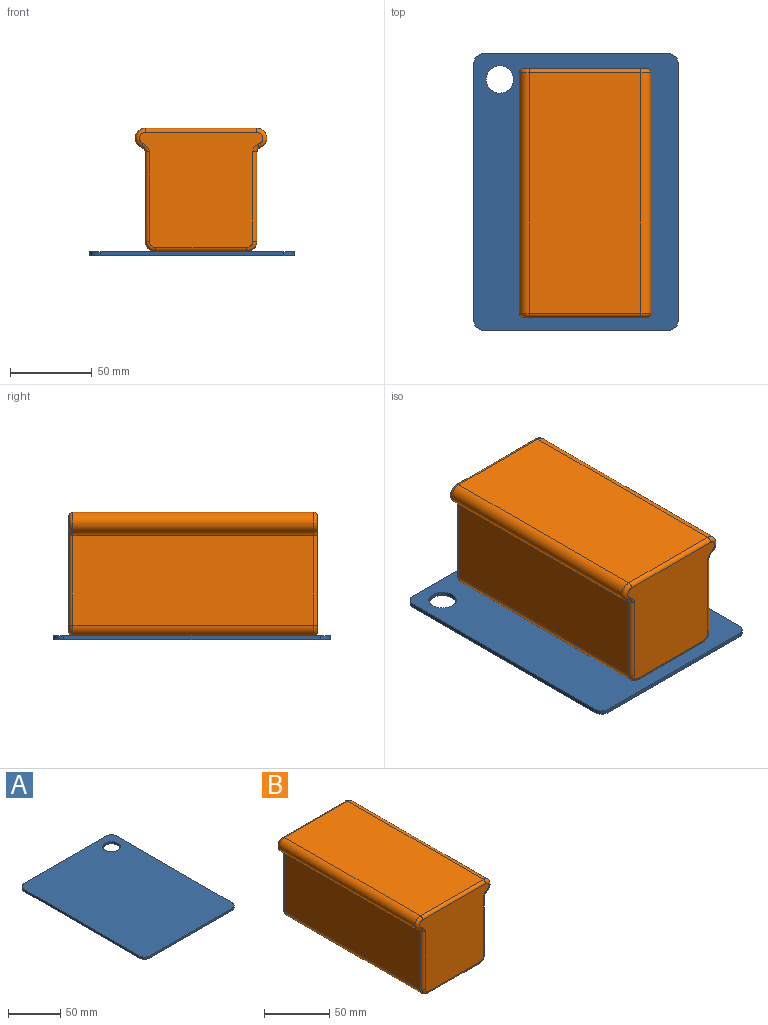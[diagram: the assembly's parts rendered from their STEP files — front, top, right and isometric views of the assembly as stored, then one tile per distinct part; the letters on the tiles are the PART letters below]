
ASSEMBLY  parts=2 mates=1
PART A: 11 faces, bbox 125.4x169.9x2.5 mm
  f0: plane 157.15x2.54mm, normal (1,0,0), area 399.2mm2, adj f1,f7,f9,f10
  f1: cylinder r=6.35mm len=6.35mm, axis (0,0,-1), area 25.3mm2, adj f0,f2,f9,f10
  f2: plane 112.7x2.54mm, normal (0,1,0), area 286.2mm2, adj f1,f3,f9,f10
  f3: cylinder r=6.35mm len=6.35mm, axis (0,0,-1), area 25.3mm2, adj f2,f4,f9,f10
  f4: plane 157.15x2.54mm, normal (-1,0,0), area 399.2mm2, adj f3,f5,f9,f10
  f5: cylinder r=6.35mm len=6.35mm, axis (0,0,-1), area 25.3mm2, adj f4,f6,f9,f10
  f6: plane 112.7x2.54mm, normal (0,-1,0), area 286.2mm2, adj f5,f7,f9,f10
  f7: cylinder r=6.35mm len=6.35mm, axis (0,0,-1), area 25.3mm2, adj f0,f6,f9,f10
  f8: cylinder r=8.36mm len=16.72mm, axis (0,0,-1), area 133.4mm2, adj f9,f10
  f9: plane 169.85x125.4mm, normal (0,0,1), area 21044.7mm2, adj f0,f1,f2,f3,f4,f5,f6,f7
  f10: plane 169.85x125.4mm, normal (0,0,-1), area 21044.7mm2, adj f0,f1,f2,f3,f4,f5,f6,f7
PART B: 32 faces, bbox 81.7x152.4x76.6 mm
  f0: cylinder r=4.63mm len=147.32mm, axis (0,-1,0), area 517.9mm2, adj f1,f9,f17,f27
  f1: plane 147.32x54.94mm, normal (-1,0,0), area 8093.7mm2, adj f0,f2,f15,f25
  f2: cylinder r=6.35mm len=147.32mm, axis (0,-1,0), area 1469.5mm2, adj f1,f3,f13,f23
  f3: plane 147.32x55.73mm, normal (0,0,-1), area 8209.8mm2, adj f2,f4,f12,f22
  f4: cylinder r=6.35mm len=147.32mm, axis (0,-1,0), area 1469.5mm2, adj f3,f5,f14,f24
  f5: plane 147.32x54.94mm, normal (1,0,0), area 8093.7mm2, adj f4,f6,f16,f26
  f6: cylinder r=3.36mm len=147.32mm, axis (0,-1,0), area 434.1mm2, adj f5,f7,f18,f28
  f7: cylinder r=6.11mm len=147.32mm, axis (0,-1,0), area 2577.6mm2, adj f6,f8,f20,f30
  f8: plane 147.32x68.43mm, normal (0,0,1), area 10080.8mm2, adj f7,f9,f21,f31
  f9: cylinder r=6.11mm len=147.32mm, axis (0,-1,0), area 2477.4mm2, adj f0,f8,f19,f29
  f10: plane 75.56x70.51mm, normal (0,1,0), area 4546.1mm2, adj f22,f23,f24,f25,f26,f27,f28,f29
  f11: plane 75.56x70.51mm, normal (0,-1,0), area 4546.1mm2, adj f12,f13,f14,f15,f16,f17,f18,f19
  f12: cylinder r=2.54mm len=55.73mm, axis (1,0,0), area 222.3mm2, adj f3,f11,f13,f14
  f13: torus R=3.81mm, axis (0,-1,0), area 34mm2, adj f2,f11,f12,f15
  f14: torus R=3.81mm, axis (0,-1,0), area 34mm2, adj f4,f11,f12,f16
  f15: cylinder r=2.54mm len=55.35mm, axis (0,0,-1), area 219.8mm2, adj f1,f11,f13,f17
  f16: cylinder r=2.54mm len=55.14mm, axis (0,0,1), area 219.5mm2, adj f5,f11,f14,f18
  f17: torus R=7.17mm, axis (0,-1,0), area 17.7mm2, adj f0,f11,f15,f19
  f18: torus R=5.9mm, axis (0,-1,0), area 15.9mm2, adj f6,f11,f16,f20
  f19: torus R=3.57mm, axis (0,-1,0), area 57.1mm2, adj f9,f11,f17,f21
  f20: torus R=3.57mm, axis (0,-1,0), area 59.6mm2, adj f7,f11,f18,f21
  f21: cylinder r=2.54mm len=68.43mm, axis (-1,0,0), area 273mm2, adj f8,f11,f19,f20
  f22: cylinder r=2.54mm len=55.73mm, axis (-1,0,0), area 222.3mm2, adj f3,f10,f23,f24
  f23: torus R=3.81mm, axis (0,-1,0), area 34mm2, adj f2,f10,f22,f25
  f24: torus R=3.81mm, axis (0,-1,0), area 34mm2, adj f4,f10,f22,f26
  f25: cylinder r=2.54mm len=55.35mm, axis (0,0,1), area 219.8mm2, adj f1,f10,f23,f27
  f26: cylinder r=2.54mm len=55.14mm, axis (0,0,-1), area 219.5mm2, adj f5,f10,f24,f28
  f27: torus R=7.17mm, axis (0,-1,0), area 17.7mm2, adj f0,f10,f25,f29
  f28: torus R=5.9mm, axis (0,-1,0), area 15.9mm2, adj f6,f10,f26,f30
  f29: torus R=3.57mm, axis (0,-1,0), area 57.1mm2, adj f9,f10,f27,f31
  f30: torus R=3.57mm, axis (0,-1,0), area 59.6mm2, adj f7,f10,f28,f31
  f31: cylinder r=2.54mm len=68.43mm, axis (1,0,0), area 273mm2, adj f8,f10,f29,f30
PLACE A rot(axis=(0,1,0),180deg) t=(8.03,-14.45,2.54)mm
PLACE B t=(5.08,0,34.22)mm
MATE fastened B.f3 <-> A.f10  axis (0,0,-1) through (5.08,0,2.54)mm
